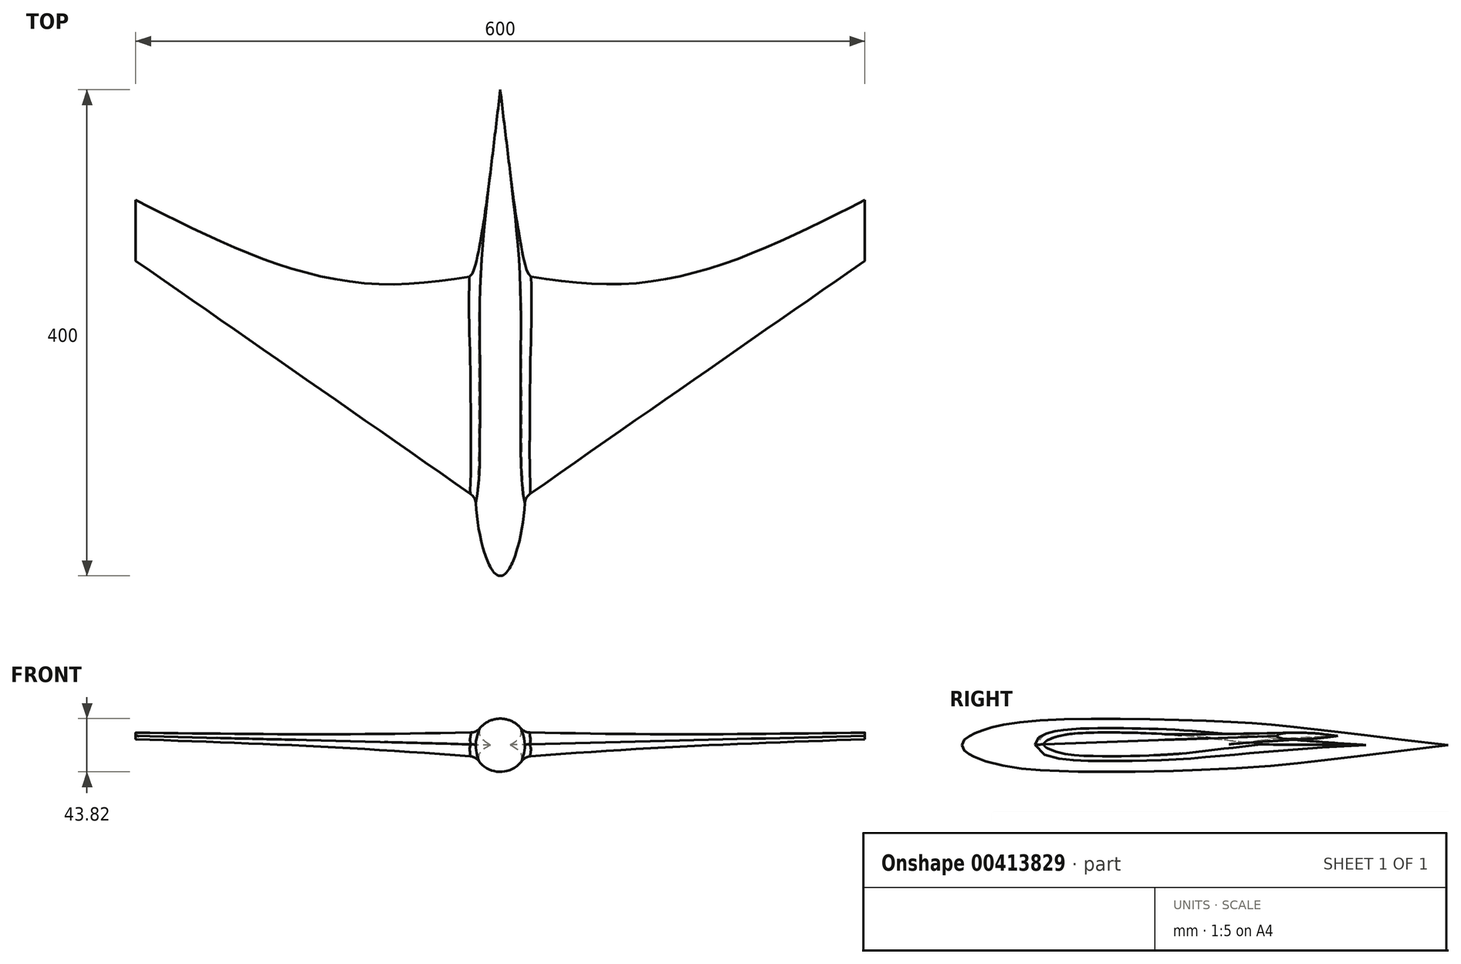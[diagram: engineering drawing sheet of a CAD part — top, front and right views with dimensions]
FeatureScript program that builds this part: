
annotation { "Feature Type Name" : "Feature", "Feature Type Description" : "" }
export const myFeature = defineFeature(function(context is Context, id is Id, definition is map)
    precondition{}
    {
        {
            assignVariable(context, id + "F0", {"name" : "l", "anyValue" : 100});
        }
        {
            var Q0;
            Q0=qCreatedBy(makeId("Right.planeOp"),FACE);
            var sketch = newSketch(context, id + "F1", { "sketchPlane" : qUnion([Q0])});
            skFitSpline(sketch, "E0", {"points": [v(99.95, 0) * mm, v(11.44, 9.5) * mm, v(-73.64, 9.79) * mm, v(-92.92, 5.64) * mm, v(-97.72, 3.3) * mm, v(-100.05, 0) * mm], "startDerivative": vector(-490.7, 57.33) * mm, "endDerivative": vector(-2.18, -61.68) * mm});
            skLineSegment(sketch, "E1", {"start": v(-12.5, 0) * mm, "end": v(-68.5, 0) * mm, "construction": true});
            skFitSpline(sketch, "E2.MirrorCS", {"points": [v(99.95, 0) * mm, v(11.44, -9.5) * mm, v(-73.64, -9.79) * mm, v(-92.92, -5.64) * mm, v(-97.72, -3.3) * mm, v(-100.05, 0) * mm], "startDerivative": vector(-490.7, -57.33) * mm, "endDerivative": vector(-2.18, 61.68) * mm});
            skSolve(sketch);
        }
        {
            var Q0;
            Q0=qCreatedBy(makeId("Right.planeOp"),FACE);
            cPlane(context, id + "F2", {"entities" : qUnion([Q0]), "cplaneType" : CPlaneType.OFFSET, "offset" : (3 * getVariable(context, 'l')) * mm, "width" : 150 * mm, "height" : 150 * mm});
        }
        {
            var Q0;
            Q0=qCreatedBy(id+"F2.planeOp",FACE);
            var sketch = newSketch(context, id + "F3", { "sketchPlane" : qUnion([Q0])});
            skFitSpline(sketch, "E3", {"points": [v(158.89, 7.57) * mm, v(136.76, 9.94) * mm, v(115.49, 10.01) * mm, v(110.67, 8.98) * mm, v(109.47, 8.4) * mm, v(108.89, 7.57) * mm], "startDerivative": vector(-122.68, 14.33) * mm, "endDerivative": vector(-0.55, -15.42) * mm});
            skLineSegment(sketch, "E4", {"start": v(130.77, 7.57) * mm, "end": v(116.77, 7.57) * mm, "construction": true});
            skFitSpline(sketch, "E5.MirrorCS", {"points": [v(158.89, 7.57) * mm, v(136.76, 5.2) * mm, v(115.49, 5.12) * mm, v(110.67, 6.16) * mm, v(109.47, 6.74) * mm, v(108.89, 7.57) * mm], "startDerivative": vector(-122.68, -14.33) * mm, "endDerivative": vector(-0.55, 15.42) * mm});
            skSolve(sketch);
        }
        {
            var Q0;
            Q0=sQuery(id+"F1.wireOp",VERTEX,"E1.start");
            var Q1;
            Q1=sQuery(id+"F1.wireOp",VERTEX,"E1.end");
            var Q2;
            Q2=sQuery(id+"F3.wireOp",VERTEX,"E4.end");
            cPlane(context, id + "F4", {"entities" : qUnion([Q0, Q1, Q2]), "cplaneType" : CPlaneType.THREE_POINT, "offset" : 25 * mm, "width" : 150 * mm, "height" : 150 * mm});
        }
        {
            var Q0;
            Q0=qCreatedBy(makeId("Right.planeOp"),FACE);
            cPlane(context, id + "F5", {"entities" : qUnion([Q0]), "cplaneType" : CPlaneType.OFFSET, "offset" : 100 * mm, "width" : 150 * mm, "height" : 150 * mm});
        }
        {
            var Q0;
            Q0=qCreatedBy(id+"F5.planeOp",FACE);
            var sketch = newSketch(context, id + "F6", { "sketchPlane" : qUnion([Q0])});
            skFitSpline(sketch, "E6", {"points": [v(89.78, 2.66) * mm, v(36.67, 8.37) * mm, v(-14.38, 8.53) * mm, v(-25.95, 6.05) * mm, v(-28.83, 4.64) * mm, v(-30.22, 2.66) * mm], "startDerivative": vector(-294.42, 34.4) * mm, "endDerivative": vector(-1.31, -37) * mm});
            skLineSegment(sketch, "E7", {"start": v(22.3, 2.66) * mm, "end": v(-11.3, 2.66) * mm, "construction": true});
            skFitSpline(sketch, "E8.MirrorCS", {"points": [v(89.78, 2.66) * mm, v(36.67, -3.05) * mm, v(-14.38, -3.21) * mm, v(-25.95, -0.73) * mm, v(-28.83, 0.68) * mm, v(-30.22, 2.66) * mm], "startDerivative": vector(-294.42, -34.4) * mm, "endDerivative": vector(-1.31, 37) * mm});
            skSolve(sketch);
        }
        {
            var Q0;
            Q0=makeQuery(id+"F1.imprint","IMPRINT",FACE,{"disambiguationData":[TD([[makeQuery(id+"F1.imprint","IMPRINT",EDGE,{"derivedFrom":sQuery(id+"F1.wireOp",EDGE,"E0")}),1.0]])]});
            var Q1;
            Q1=makeQuery(id+"F6.imprint","IMPRINT",FACE,{"disambiguationData":[TD([[makeQuery(id+"F6.imprint","IMPRINT",EDGE,{"derivedFrom":sQuery(id+"F6.wireOp",EDGE,"E6")}),1.0]])]});
            var Q2;
            Q2=makeQuery(id+"F3.imprint","IMPRINT",FACE,{"disambiguationData":[TD([[makeQuery(id+"F3.imprint","IMPRINT",EDGE,{"derivedFrom":sQuery(id+"F3.wireOp",EDGE,"E3")}),1.0]])]});
            loft(context, id + "F7", {"sheetProfilesArray" : [{ "sheetProfileEntities" : qUnion([Q0]) }, { "sheetProfileEntities" : qUnion([Q1]) }, { "sheetProfileEntities" : qUnion([Q2]) }]});
        }
        {
            var Q0;
            Q0=makeQuery(id+"F7.opLoft","SWEPT_BODY",BODY,{"disambiguationData":[OSD([makeQuery(id+"F1.imprint","IMPRINT",FACE,{"disambiguationData":[TD([[makeQuery(id+"F1.imprint","IMPRINT",EDGE,{"derivedFrom":sQuery(id+"F1.wireOp",EDGE,"E0")}),1.0]])]}),makeQuery(id+"F3.imprint","IMPRINT",FACE,{"disambiguationData":[TD([[makeQuery(id+"F3.imprint","IMPRINT",EDGE,{"derivedFrom":sQuery(id+"F3.wireOp",EDGE,"E3")}),1.0]])]})])]});
            var Q1;
            Q1=makeQuery(id+"F1.imprint","IMPRINT",FACE,{"disambiguationData":[TD([[makeQuery(id+"F1.imprint","IMPRINT",EDGE,{"derivedFrom":sQuery(id+"F1.wireOp",EDGE,"E0")}),1.0]])]});
            mirror(context, id + "F8", {"entities" : qUnion([Q0]), "mirrorPlane" : qUnion([Q1])});
        }
        {
            var Q0;
            Q0=qCreatedBy(makeId("Right.planeOp"),FACE);
            var sketch = newSketch(context, id + "F9", { "sketchPlane" : qUnion([Q0])});
            skFitSpline(sketch, "E9", {"points": [v(249.67, -0.05) * mm, v(72.65, 18.96) * mm, v(-97.52, 19.52) * mm, v(-136.08, 11.23) * mm, v(-145.67, 6.55) * mm, v(-150.33, -0.05) * mm], "startDerivative": vector(-981.41, 114.66) * mm, "endDerivative": vector(-4.37, -123.36) * mm});
            skLineSegment(sketch, "E10", {"start": v(-150.33, -0.05) * mm, "end": v(249.67, -0.05) * mm});
            skSolve(sketch);
        }
        {
            var Q0;
            Q0=makeQuery(id+"F9.imprint","IMPRINT",FACE,{"disambiguationData":[TD([[makeQuery(id+"F9.imprint","IMPRINT",EDGE,{"derivedFrom":sQuery(id+"F9.wireOp",EDGE,"E9")}),1.0]])]});
            var Q1;
            Q1=sQuery(id+"F9.wireOp",EDGE,"E10");
            revolve(context, id + "F10", {"entities" : qUnion([Q0]), "axis" : qUnion([Q1]), "revolveType" : RevolveType.FULL});
        }
        {
            var Q0;
            Q0=makeQuery(id+"F10.opRevolve","SWEPT_BODY",BODY,{"disambiguationData":[OSD([sQuery(id+"F9.wireOp",EDGE,"E9"),sQuery(id+"F9.wireOp",EDGE,"E10")])]});
            var Q1;
            Q1=makeQuery(id+"F8.opPattern","COPY",BODY,{"derivedFrom":makeQuery(id+"F7.opLoft","SWEPT_BODY",BODY,{"disambiguationData":[OSD([makeQuery(id+"F1.imprint","IMPRINT",FACE,{"disambiguationData":[TD([[makeQuery(id+"F1.imprint","IMPRINT",EDGE,{"derivedFrom":sQuery(id+"F1.wireOp",EDGE,"E0")}),1.0]])]}),makeQuery(id+"F3.imprint","IMPRINT",FACE,{"disambiguationData":[TD([[makeQuery(id+"F3.imprint","IMPRINT",EDGE,{"derivedFrom":sQuery(id+"F3.wireOp",EDGE,"E3")}),1.0]])]}),sQuery(id+"F6.wireOp",EDGE,"E8.MirrorCS")])]}),"instanceName":"1"});
            var Q2;
            Q2=makeQuery(id+"F7.opLoft","SWEPT_BODY",BODY,{"disambiguationData":[OSD([makeQuery(id+"F1.imprint","IMPRINT",FACE,{"disambiguationData":[TD([[makeQuery(id+"F1.imprint","IMPRINT",EDGE,{"derivedFrom":sQuery(id+"F1.wireOp",EDGE,"E0")}),1.0]])]}),makeQuery(id+"F3.imprint","IMPRINT",FACE,{"disambiguationData":[TD([[makeQuery(id+"F3.imprint","IMPRINT",EDGE,{"derivedFrom":sQuery(id+"F3.wireOp",EDGE,"E3")}),1.0]])]}),sQuery(id+"F6.wireOp",EDGE,"E8.MirrorCS")])]});
            booleanBodies(context, id + "F11", {"operationType" : BooleanOperationType.UNION, "tools" : qUnion([Q0, Q1, Q2])});
        }
        {
            var Q0;
            {var subQ0=sQuery(id+"F6.wireOp",EDGE,"E6");var subQ1=sQuery(id+"F6.wireOp",EDGE,"E8.MirrorCS");var subQ2=sQuery(id+"F1.wireOp",EDGE,"E0");var subQ3=sQuery(id+"F1.wireOp",EDGE,"E2.MirrorCS");Q0=makeQuery(id+"F11.opBoolean","INTERSECT",EDGE,{"derivedFrom":[makeQuery(id+"F8.opPattern","COPY",FACE,{"derivedFrom":makeQuery(id+"F7.opLoft","SWEPT_FACE",FACE,{"disambiguationData":[OSD([subQ2,subQ3,subQ0,subQ1]),TDD([makeQuery(id+"F1.imprint","INTERSECT",VERTEX,{"disambiguationData":[OD(0.0)],"derivedFrom":[subQ2,subQ3]}),makeQuery(id+"F1.imprint","INTERSECT",VERTEX,{"disambiguationData":[OD(1.0)],"derivedFrom":[subQ2,subQ3]}),makeQuery(id+"F1.imprint","IMPRINT",EDGE,{"derivedFrom":subQ2}),makeQuery(id+"F6.imprint","INTERSECT",VERTEX,{"disambiguationData":[OD(0.0)],"derivedFrom":[subQ0,subQ1]}),makeQuery(id+"F6.imprint","INTERSECT",VERTEX,{"disambiguationData":[OD(1.0)],"derivedFrom":[subQ0,subQ1]}),makeQuery(id+"F6.imprint","IMPRINT",EDGE,{"derivedFrom":subQ0})])]}),"instanceName":"1"}),makeQuery(id+"F10.opRevolve","SWEPT_FACE",FACE,{"disambiguationData":[OSD([sQuery(id+"F9.wireOp",EDGE,"E9")])]})]});}
            var Q1;
            {var subQ0=sQuery(id+"F6.wireOp",EDGE,"E8.MirrorCS");var subQ1=sQuery(id+"F6.wireOp",EDGE,"E6");var subQ2=sQuery(id+"F1.wireOp",EDGE,"E2.MirrorCS");var subQ3=sQuery(id+"F1.wireOp",EDGE,"E0");Q1=makeQuery(id+"F11.opBoolean","INTERSECT",EDGE,{"derivedFrom":[makeQuery(id+"F8.opPattern","COPY",FACE,{"derivedFrom":makeQuery(id+"F7.opLoft","SWEPT_FACE",FACE,{"disambiguationData":[OSD([subQ3,subQ2,subQ1,subQ0]),TDD([makeQuery(id+"F1.imprint","INTERSECT",VERTEX,{"disambiguationData":[OD(0.0)],"derivedFrom":[subQ3,subQ2]}),makeQuery(id+"F1.imprint","INTERSECT",VERTEX,{"disambiguationData":[OD(1.0)],"derivedFrom":[subQ3,subQ2]}),makeQuery(id+"F1.imprint","IMPRINT",EDGE,{"derivedFrom":subQ2}),makeQuery(id+"F6.imprint","INTERSECT",VERTEX,{"disambiguationData":[OD(0.0)],"derivedFrom":[subQ1,subQ0]}),makeQuery(id+"F6.imprint","INTERSECT",VERTEX,{"disambiguationData":[OD(1.0)],"derivedFrom":[subQ1,subQ0]}),makeQuery(id+"F6.imprint","IMPRINT",EDGE,{"derivedFrom":subQ0})])]}),"instanceName":"1"}),makeQuery(id+"F10.opRevolve","SWEPT_FACE",FACE,{"disambiguationData":[OSD([sQuery(id+"F9.wireOp",EDGE,"E9")])]})]});}
            var Q2;
            {var subQ0=sQuery(id+"F6.wireOp",EDGE,"E6");var subQ1=sQuery(id+"F6.wireOp",EDGE,"E8.MirrorCS");var subQ2=sQuery(id+"F1.wireOp",EDGE,"E0");var subQ3=sQuery(id+"F1.wireOp",EDGE,"E2.MirrorCS");Q2=makeQuery(id+"F11.opBoolean","INTERSECT",EDGE,{"derivedFrom":[makeQuery(id+"F7.opLoft","SWEPT_FACE",FACE,{"disambiguationData":[OSD([subQ2,subQ3,subQ0,subQ1]),TDD([makeQuery(id+"F1.imprint","INTERSECT",VERTEX,{"disambiguationData":[OD(0.0)],"derivedFrom":[subQ2,subQ3]}),makeQuery(id+"F1.imprint","INTERSECT",VERTEX,{"disambiguationData":[OD(1.0)],"derivedFrom":[subQ2,subQ3]}),makeQuery(id+"F1.imprint","IMPRINT",EDGE,{"derivedFrom":subQ2}),makeQuery(id+"F6.imprint","INTERSECT",VERTEX,{"disambiguationData":[OD(0.0)],"derivedFrom":[subQ0,subQ1]}),makeQuery(id+"F6.imprint","INTERSECT",VERTEX,{"disambiguationData":[OD(1.0)],"derivedFrom":[subQ0,subQ1]}),makeQuery(id+"F6.imprint","IMPRINT",EDGE,{"derivedFrom":subQ0})])]}),makeQuery(id+"F10.opRevolve","SWEPT_FACE",FACE,{"disambiguationData":[OSD([sQuery(id+"F9.wireOp",EDGE,"E9")])]})]});}
            var Q3;
            {var subQ0=sQuery(id+"F6.wireOp",EDGE,"E8.MirrorCS");var subQ1=sQuery(id+"F6.wireOp",EDGE,"E6");var subQ2=sQuery(id+"F1.wireOp",EDGE,"E2.MirrorCS");var subQ3=sQuery(id+"F1.wireOp",EDGE,"E0");Q3=makeQuery(id+"F11.opBoolean","INTERSECT",EDGE,{"derivedFrom":[makeQuery(id+"F7.opLoft","SWEPT_FACE",FACE,{"disambiguationData":[OSD([subQ3,subQ2,subQ1,subQ0]),TDD([makeQuery(id+"F1.imprint","INTERSECT",VERTEX,{"disambiguationData":[OD(0.0)],"derivedFrom":[subQ3,subQ2]}),makeQuery(id+"F1.imprint","INTERSECT",VERTEX,{"disambiguationData":[OD(1.0)],"derivedFrom":[subQ3,subQ2]}),makeQuery(id+"F1.imprint","IMPRINT",EDGE,{"derivedFrom":subQ2}),makeQuery(id+"F6.imprint","INTERSECT",VERTEX,{"disambiguationData":[OD(0.0)],"derivedFrom":[subQ1,subQ0]}),makeQuery(id+"F6.imprint","INTERSECT",VERTEX,{"disambiguationData":[OD(1.0)],"derivedFrom":[subQ1,subQ0]}),makeQuery(id+"F6.imprint","IMPRINT",EDGE,{"derivedFrom":subQ0})])]}),makeQuery(id+"F10.opRevolve","SWEPT_FACE",FACE,{"disambiguationData":[OSD([sQuery(id+"F9.wireOp",EDGE,"E9")])]})]});}
            fillet(context, id + "F12", {"entities" : qUnion([Q0, Q1, Q2, Q3]), "radius" : 10 * mm, "tangentPropagation" : true, "allowEdgeOverflow" : false});
        }
    });
